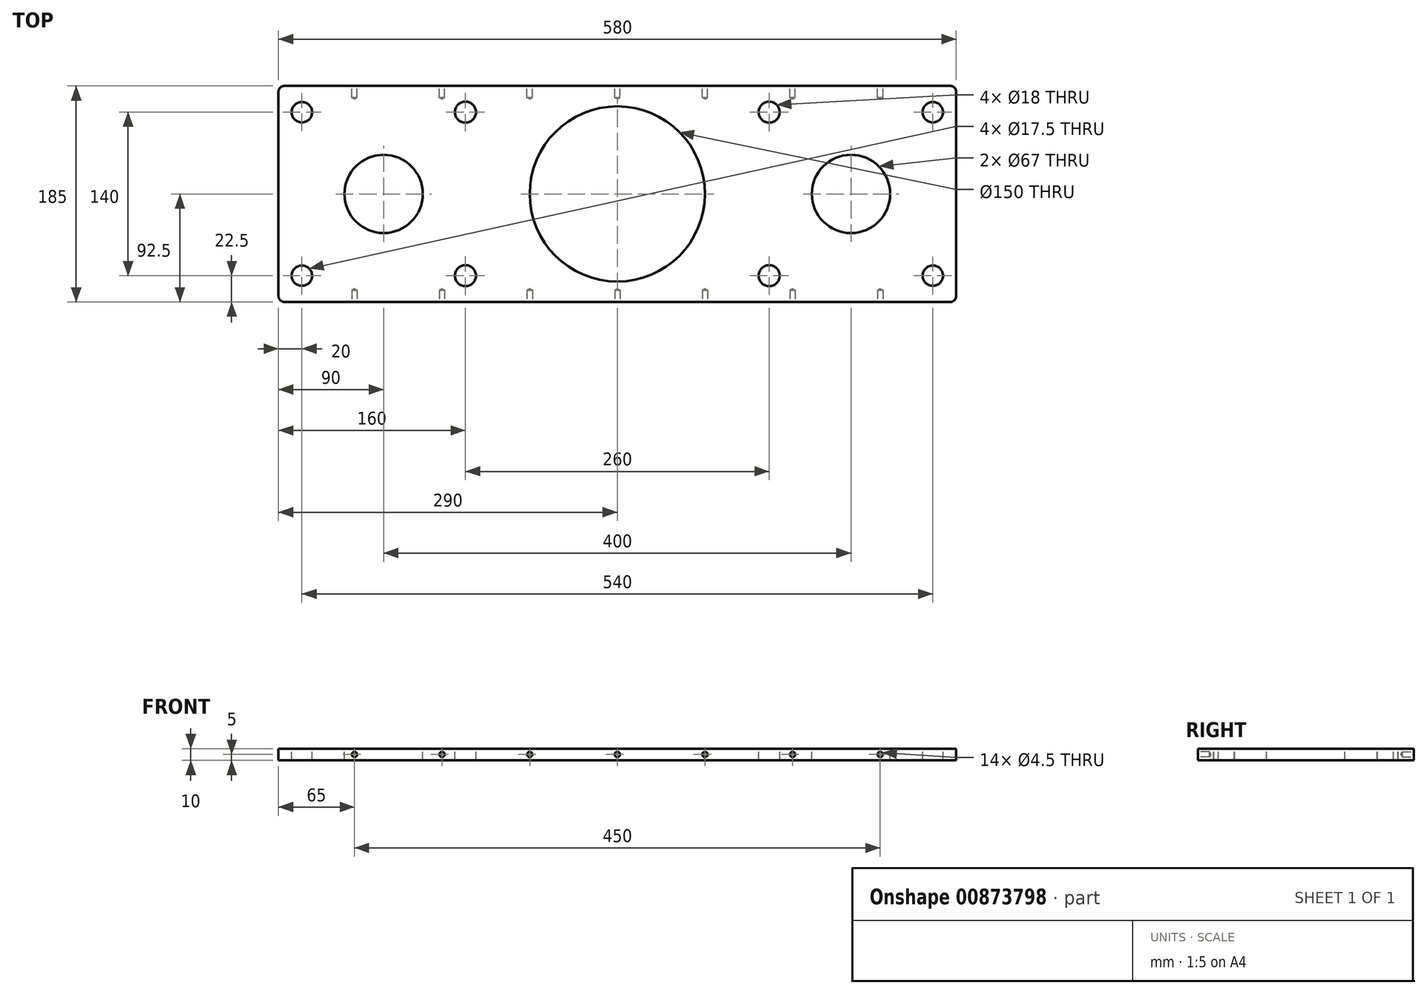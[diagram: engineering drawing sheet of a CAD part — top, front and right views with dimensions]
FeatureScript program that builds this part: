
annotation { "Feature Type Name" : "Feature", "Feature Type Description" : "" }
export const myFeature = defineFeature(function(context is Context, id is Id, definition is map)
    precondition{}
    {
        {
            var Q0;
            Q0=qCreatedBy(makeId("Top.planeOp"),FACE);
            var sketch = newSketch(context, id + "F0", { "sketchPlane" : qUnion([Q0])});
            skLineSegment(sketch, "E0.bottom", {"start": v(290, -92.5) * mm, "end": v(-290, -92.5) * mm});
            skLineSegment(sketch, "E0.top", {"start": v(290, 92.5) * mm, "end": v(-290, 92.5) * mm});
            skLineSegment(sketch, "E0.left", {"start": v(290, -92.5) * mm, "end": v(290, 92.5) * mm});
            skLineSegment(sketch, "E0.right", {"start": v(-290, -92.5) * mm, "end": v(-290, 92.5) * mm});
            skPoint(sketch, "E0.middle", {"position": v(0, 0) * mm});
            skLineSegment(sketch, "E1.bottom", {"start": v(-270, -70) * mm, "end": v(-130, -70) * mm});
            skLineSegment(sketch, "E1.top", {"start": v(-270, 70) * mm, "end": v(-130, 70) * mm});
            skLineSegment(sketch, "E1.left", {"start": v(-270, -70) * mm, "end": v(-270, 70) * mm});
            skLineSegment(sketch, "E1.right", {"start": v(-130, -70) * mm, "end": v(-130, 70) * mm, "construction": true});
            skPoint(sketch, "E1.middle", {"position": v(-200, 0) * mm});
            skLineSegment(sketch, "E2.bottom", {"start": v(130, -70) * mm, "end": v(270, -70) * mm});
            skLineSegment(sketch, "E2.top", {"start": v(130, 70) * mm, "end": v(270, 70) * mm});
            skLineSegment(sketch, "E2.left", {"start": v(130, -70) * mm, "end": v(130, 70) * mm, "construction": true});
            skLineSegment(sketch, "E2.right", {"start": v(270, -70) * mm, "end": v(270, 70) * mm});
            skPoint(sketch, "E2.middle", {"position": v(200, 0) * mm});
            skCircle(sketch, "E3", {"center": v(-200, 0) * mm, "radius": 33.5 * mm});
            skCircle(sketch, "E4", {"center": v(200, 0) * mm, "radius": 33.5 * mm});
            skCircle(sketch, "E5", {"center": v(130, 70) * mm, "radius": 9 * mm});
            skCircle(sketch, "E6", {"center": v(130, -70) * mm, "radius": 9 * mm});
            skCircle(sketch, "E7", {"center": v(270, -70) * mm, "radius": 9 * mm});
            skCircle(sketch, "E8", {"center": v(270, 70) * mm, "radius": 9 * mm});
            skCircle(sketch, "E9", {"center": v(-270, 70) * mm, "radius": 9 * mm});
            skCircle(sketch, "E10", {"center": v(-130, 70) * mm, "radius": 9 * mm});
            skCircle(sketch, "E11", {"center": v(-130, -70) * mm, "radius": 9 * mm});
            skCircle(sketch, "E12", {"center": v(-270, -70) * mm, "radius": 9 * mm});
            skCircle(sketch, "E13", {"center": v(0, 0) * mm, "radius": 75 * mm});
            skLineSegment(sketch, "E14", {"start": v(-200, 0) * mm, "end": v(0, 0) * mm, "construction": true});
            skLineSegment(sketch, "E15", {"start": v(200, 0) * mm, "end": v(0, 0) * mm});
            skCircle(sketch, "E16", {"center": v(0, 0) * mm, "radius": 88.5 * mm, "construction": true});
            skSolve(sketch);
        }
        {
            var Q0;
            Q0=makeQuery(id+"F0.imprint","IMPRINT",FACE,{"disambiguationData":[TD([[makeQuery(id+"F0.imprint","IMPRINT",EDGE,{"derivedFrom":sQuery(id+"F0.wireOp",EDGE,"E0.bottom")}),-1.0]])]});
            var Q1;
            {var subQ0=sQuery(id+"F0.wireOp",EDGE,"E1.right");var subQ1=sQuery(id+"F0.wireOp",EDGE,"E1.top");var subQ2=makeQuery(id+"F0.imprint","INTERSECT",VERTEX,{"derivedFrom":[subQ1,subQ0]});Q1=makeQuery(id+"F0.imprint","IMPRINT",FACE,{"disambiguationData":[TD([[makeQuery(id+"F0.imprint","IMPRINT",EDGE,{"disambiguationData":[TD([[subQ2,1.0]])],"derivedFrom":subQ1}),1.0]])]});}
            var Q2;
            Q2=makeQuery(id+"F0.imprint","IMPRINT",FACE,{"disambiguationData":[TD([[makeQuery(id+"F0.imprint","IMPRINT",EDGE,{"derivedFrom":sQuery(id+"F0.wireOp",EDGE,"E3")}),-1.0]])]});
            var Q3;
            {var subQ0=sQuery(id+"F0.wireOp",EDGE,"E1.left");var subQ1=sQuery(id+"F0.wireOp",EDGE,"E1.top");var subQ2=makeQuery(id+"F0.imprint","INTERSECT",VERTEX,{"derivedFrom":[subQ1,subQ0]});Q3=makeQuery(id+"F0.imprint","IMPRINT",FACE,{"disambiguationData":[TD([[makeQuery(id+"F0.imprint","IMPRINT",EDGE,{"disambiguationData":[TD([[subQ2,-1.0]])],"derivedFrom":subQ1}),1.0]])]});}
            var Q4;
            {var subQ0=sQuery(id+"F0.wireOp",EDGE,"E1.left");var subQ1=sQuery(id+"F0.wireOp",EDGE,"E1.top");var subQ2=makeQuery(id+"F0.imprint","INTERSECT",VERTEX,{"derivedFrom":[subQ1,subQ0]});Q4=makeQuery(id+"F0.imprint","IMPRINT",FACE,{"disambiguationData":[TD([[makeQuery(id+"F0.imprint","IMPRINT",EDGE,{"disambiguationData":[TD([[subQ2,-1.0]])],"derivedFrom":subQ1}),-1.0]])]});}
            var Q5;
            {var subQ0=sQuery(id+"F0.wireOp",EDGE,"E1.right");var subQ1=sQuery(id+"F0.wireOp",EDGE,"E1.top");var subQ2=makeQuery(id+"F0.imprint","INTERSECT",VERTEX,{"derivedFrom":[subQ1,subQ0]});Q5=makeQuery(id+"F0.imprint","IMPRINT",FACE,{"disambiguationData":[TD([[makeQuery(id+"F0.imprint","IMPRINT",EDGE,{"disambiguationData":[TD([[subQ2,1.0]])],"derivedFrom":subQ1}),-1.0]])]});}
            var Q6;
            {var subQ0=sQuery(id+"F0.wireOp",EDGE,"E1.right");var subQ1=sQuery(id+"F0.wireOp",EDGE,"E1.bottom");var subQ2=makeQuery(id+"F0.imprint","INTERSECT",VERTEX,{"derivedFrom":[subQ1,subQ0]});Q6=makeQuery(id+"F0.imprint","IMPRINT",FACE,{"disambiguationData":[TD([[makeQuery(id+"F0.imprint","IMPRINT",EDGE,{"disambiguationData":[TD([[subQ2,1.0]])],"derivedFrom":subQ1}),-1.0]])]});}
            var Q7;
            {var subQ0=sQuery(id+"F0.wireOp",EDGE,"E1.left");var subQ1=sQuery(id+"F0.wireOp",EDGE,"E1.bottom");var subQ2=makeQuery(id+"F0.imprint","INTERSECT",VERTEX,{"derivedFrom":[subQ1,subQ0]});Q7=makeQuery(id+"F0.imprint","IMPRINT",FACE,{"disambiguationData":[TD([[makeQuery(id+"F0.imprint","IMPRINT",EDGE,{"disambiguationData":[TD([[subQ2,-1.0]])],"derivedFrom":subQ1}),1.0]])]});}
            var Q8;
            {var subQ0=sQuery(id+"F0.wireOp",EDGE,"E2.right");var subQ1=sQuery(id+"F0.wireOp",EDGE,"E2.top");var subQ2=makeQuery(id+"F0.imprint","INTERSECT",VERTEX,{"derivedFrom":[subQ1,subQ0]});Q8=makeQuery(id+"F0.imprint","IMPRINT",FACE,{"disambiguationData":[TD([[makeQuery(id+"F0.imprint","IMPRINT",EDGE,{"disambiguationData":[TD([[subQ2,1.0]])],"derivedFrom":subQ1}),-1.0]])]});}
            var Q9;
            {var subQ0=sQuery(id+"F0.wireOp",EDGE,"E2.left");var subQ1=sQuery(id+"F0.wireOp",EDGE,"E2.top");var subQ2=makeQuery(id+"F0.imprint","INTERSECT",VERTEX,{"derivedFrom":[subQ1,subQ0]});Q9=makeQuery(id+"F0.imprint","IMPRINT",FACE,{"disambiguationData":[TD([[makeQuery(id+"F0.imprint","IMPRINT",EDGE,{"disambiguationData":[TD([[subQ2,-1.0]])],"derivedFrom":subQ1}),-1.0]])]});}
            var Q10;
            {var subQ0=sQuery(id+"F0.wireOp",EDGE,"E2.left");var subQ1=sQuery(id+"F0.wireOp",EDGE,"E2.bottom");var subQ2=makeQuery(id+"F0.imprint","INTERSECT",VERTEX,{"derivedFrom":[subQ1,subQ0]});Q10=makeQuery(id+"F0.imprint","IMPRINT",FACE,{"disambiguationData":[TD([[makeQuery(id+"F0.imprint","IMPRINT",EDGE,{"disambiguationData":[TD([[subQ2,-1.0]])],"derivedFrom":subQ1}),-1.0]])]});}
            var Q11;
            {var subQ0=sQuery(id+"F0.wireOp",EDGE,"E2.right");var subQ1=sQuery(id+"F0.wireOp",EDGE,"E2.bottom");var subQ2=makeQuery(id+"F0.imprint","INTERSECT",VERTEX,{"derivedFrom":[subQ1,subQ0]});Q11=makeQuery(id+"F0.imprint","IMPRINT",FACE,{"disambiguationData":[TD([[makeQuery(id+"F0.imprint","IMPRINT",EDGE,{"disambiguationData":[TD([[subQ2,1.0]])],"derivedFrom":subQ1}),1.0]])]});}
            var Q12;
            {var subQ0=sQuery(id+"F0.wireOp",EDGE,"E1.right");var subQ1=sQuery(id+"F0.wireOp",EDGE,"E1.bottom");var subQ2=makeQuery(id+"F0.imprint","INTERSECT",VERTEX,{"derivedFrom":[subQ1,subQ0]});Q12=makeQuery(id+"F0.imprint","IMPRINT",FACE,{"disambiguationData":[TD([[makeQuery(id+"F0.imprint","IMPRINT",EDGE,{"disambiguationData":[TD([[subQ2,1.0]])],"derivedFrom":subQ1}),1.0]])]});}
            var Q13;
            {var subQ0=sQuery(id+"F0.wireOp",EDGE,"E1.left");var subQ1=sQuery(id+"F0.wireOp",EDGE,"E1.bottom");var subQ2=makeQuery(id+"F0.imprint","INTERSECT",VERTEX,{"derivedFrom":[subQ1,subQ0]});Q13=makeQuery(id+"F0.imprint","IMPRINT",FACE,{"disambiguationData":[TD([[makeQuery(id+"F0.imprint","IMPRINT",EDGE,{"disambiguationData":[TD([[subQ2,-1.0]])],"derivedFrom":subQ1}),-1.0]])]});}
            var Q14;
            {var subQ0=sQuery(id+"F0.wireOp",EDGE,"E2.right");var subQ1=sQuery(id+"F0.wireOp",EDGE,"E2.bottom");var subQ2=makeQuery(id+"F0.imprint","INTERSECT",VERTEX,{"derivedFrom":[subQ1,subQ0]});Q14=makeQuery(id+"F0.imprint","IMPRINT",FACE,{"disambiguationData":[TD([[makeQuery(id+"F0.imprint","IMPRINT",EDGE,{"disambiguationData":[TD([[subQ2,1.0]])],"derivedFrom":subQ1}),-1.0]])]});}
            var Q15;
            {var subQ0=sQuery(id+"F0.wireOp",EDGE,"E2.left");var subQ1=sQuery(id+"F0.wireOp",EDGE,"E2.top");var subQ2=makeQuery(id+"F0.imprint","INTERSECT",VERTEX,{"derivedFrom":[subQ1,subQ0]});Q15=makeQuery(id+"F0.imprint","IMPRINT",FACE,{"disambiguationData":[TD([[makeQuery(id+"F0.imprint","IMPRINT",EDGE,{"disambiguationData":[TD([[subQ2,-1.0]])],"derivedFrom":subQ1}),1.0]])]});}
            var Q16;
            {var subQ0=sQuery(id+"F0.wireOp",EDGE,"E2.right");var subQ1=sQuery(id+"F0.wireOp",EDGE,"E2.top");var subQ2=makeQuery(id+"F0.imprint","INTERSECT",VERTEX,{"derivedFrom":[subQ1,subQ0]});Q16=makeQuery(id+"F0.imprint","IMPRINT",FACE,{"disambiguationData":[TD([[makeQuery(id+"F0.imprint","IMPRINT",EDGE,{"disambiguationData":[TD([[subQ2,1.0]])],"derivedFrom":subQ1}),1.0]])]});}
            var Q17;
            {var subQ0=sQuery(id+"F0.wireOp",EDGE,"E2.left");var subQ1=sQuery(id+"F0.wireOp",EDGE,"E2.bottom");var subQ2=makeQuery(id+"F0.imprint","INTERSECT",VERTEX,{"derivedFrom":[subQ1,subQ0]});Q17=makeQuery(id+"F0.imprint","IMPRINT",FACE,{"disambiguationData":[TD([[makeQuery(id+"F0.imprint","IMPRINT",EDGE,{"disambiguationData":[TD([[subQ2,-1.0]])],"derivedFrom":subQ1}),1.0]])]});}
            var Q18;
            Q18=makeQuery(id+"F0.imprint","IMPRINT",FACE,{"disambiguationData":[TD([[makeQuery(id+"F0.imprint","IMPRINT",EDGE,{"derivedFrom":sQuery(id+"F0.wireOp",EDGE,"E4")}),-1.0]])]});
            var Q19;
            Q19=makeQuery(id+"F0.imprint","IMPRINT",FACE,{"disambiguationData":[TD([[makeQuery(id+"F0.imprint","IMPRINT",EDGE,{"derivedFrom":sQuery(id+"F0.wireOp",EDGE,"E13")}),-1.0]])]});
            var Q20;
            {var subQ0=sQuery(id+"F0.wireOp",EDGE,"E10");var subQ1=sQuery(id+"F0.wireOp",EDGE,"E0.top");var subQ2=makeQuery(id+"F0.imprint","INTERSECT",VERTEX,{"disambiguationData":[OD(1.0)],"derivedFrom":[subQ1,subQ0]});Q20=makeQuery(id+"F0.imprint","IMPRINT",FACE,{"disambiguationData":[TD([[makeQuery(id+"F0.imprint","IMPRINT",EDGE,{"disambiguationData":[TD([[subQ2,-1.0]])],"derivedFrom":subQ1}),1.0]])]});}
            var Q21;
            {var subQ0=sQuery(id+"F0.wireOp",EDGE,"E8");var subQ1=sQuery(id+"F0.wireOp",EDGE,"E0.top");var subQ2=makeQuery(id+"F0.imprint","INTERSECT",VERTEX,{"disambiguationData":[OD(1.0)],"derivedFrom":[subQ1,subQ0]});Q21=makeQuery(id+"F0.imprint","IMPRINT",FACE,{"disambiguationData":[TD([[makeQuery(id+"F0.imprint","IMPRINT",EDGE,{"disambiguationData":[TD([[subQ2,-1.0]])],"derivedFrom":subQ1}),1.0]])]});}
            var Q22;
            {var subQ5=sQuery(id+"F0.wireOp",EDGE,"E0.left");Q22=makeQuery(id+"F0.imprint","IMPRINT",FACE,{"disambiguationData":[TD([[makeQuery(id+"F0.imprint","IMPRINT",EDGE,{"derivedFrom":subQ5}),1.0]])]});}
            var Q23;
            {var subQ0=sQuery(id+"F0.wireOp",EDGE,"E0.right");Q23=makeQuery(id+"F0.imprint","IMPRINT",FACE,{"disambiguationData":[TD([[makeQuery(id+"F0.imprint","IMPRINT",EDGE,{"derivedFrom":subQ0}),-1.0]])]});}
            extrude(context, id + "F1", {"entities" : qUnion([Q0, Q1, Q2, Q3, Q4, Q5, Q6, Q7, Q8, Q9, Q10, Q11, Q12, Q13, Q14, Q15, Q16, Q17, Q18, Q19, Q20, Q21, Q22, Q23]), "oppositeDirection" : true, "depth" : 10 * mm, "offsetDistance" : 25 * mm});
        }
        {
            var Q0;
            Q0=sQuery(id+"F0.wireOp",VERTEX,"E1.bottom.start");
            var Q1;
            Q1=sQuery(id+"F0.wireOp",VERTEX,"E1.bottom.end");
            var Q2;
            Q2=sQuery(id+"F0.wireOp",VERTEX,"E1.top.end");
            var Q3;
            Q3=sQuery(id+"F0.wireOp",VERTEX,"E1.top.start");
            var Q4;
            Q4=sQuery(id+"F0.wireOp",VERTEX,"E2.bottom.start");
            var Q5;
            Q5=sQuery(id+"F0.wireOp",VERTEX,"E2.bottom.end");
            var Q6;
            Q6=sQuery(id+"F0.wireOp",VERTEX,"E2.top.end");
            var Q7;
            Q7=sQuery(id+"F0.wireOp",VERTEX,"E2.top.start");
            var Q8;
            Q8=makeQuery(id+"F1.opExtrude","SWEPT_BODY",BODY,{"disambiguationData":[OSD([sQuery(id+"F0.wireOp",EDGE,"E0.bottom"),sQuery(id+"F0.wireOp",EDGE,"E0.top"),sQuery(id+"F0.wireOp",EDGE,"E0.left"),sQuery(id+"F0.wireOp",EDGE,"E0.right"),sQuery(id+"F0.wireOp",EDGE,"E3"),sQuery(id+"F0.wireOp",EDGE,"E4"),sQuery(id+"F0.wireOp",EDGE,"E13")])]});
            hole(context, id + "F2", {"style" : HoleStyle.SIMPLE, "endStyle" : HoleEndStyle.BLIND, "standardTappedOrClearance" : lookupTablePath({ "fit" : "Normal", "standard" : "ISO", "size" : "M16", "type" : "Clearance" }), "standardBlindInLast" : lookupTablePath({ "fit" : "Normal", "standard" : "ISO", "engagement" : "75%", "pitch" : "2 mm", "size" : "M16", "type" : "Clearance & tapped" }), "holeDiameter" : 17.5 * mm, "majorDiameter" : 5 * mm, "holeDepth" : 16.5 * mm, "isTappedThrough" : true, "tappedDepth" : 12 * mm, "tapClearance" : 3, "locations" : qUnion([Q0, Q1, Q2, Q3, Q4, Q5, Q6, Q7]), "scope" : qUnion([Q8])});
        }
        {
            var Q0;
            Q0=makeQuery(id+"F1.opExtrude","SWEPT_EDGE",EDGE,{"disambiguationData":[OSD([sQuery(id+"F0.wireOp",EDGE,"E0.bottom"),sQuery(id+"F0.wireOp",EDGE,"E0.left")])]});
            var Q1;
            Q1=makeQuery(id+"F1.opExtrude","SWEPT_EDGE",EDGE,{"disambiguationData":[OSD([sQuery(id+"F0.wireOp",EDGE,"E0.top"),sQuery(id+"F0.wireOp",EDGE,"E0.left")])]});
            var Q2;
            Q2=makeQuery(id+"F1.opExtrude","SWEPT_EDGE",EDGE,{"disambiguationData":[OSD([sQuery(id+"F0.wireOp",EDGE,"E0.bottom"),sQuery(id+"F0.wireOp",EDGE,"E0.right")])]});
            var Q3;
            Q3=makeQuery(id+"F1.opExtrude","SWEPT_EDGE",EDGE,{"disambiguationData":[OSD([sQuery(id+"F0.wireOp",EDGE,"E0.top"),sQuery(id+"F0.wireOp",EDGE,"E0.right")])]});
            fillet(context, id + "F3", {"entities" : qUnion([Q0, Q1, Q2, Q3]), "radius" : 5 * mm, "tangentPropagation" : true, "defaultsChanged" : true, "vertexSettings" : [], "allowEdgeOverflow" : false});
        }
        {
            var Q0;
            Q0=makeQuery(id+"F1.opExtrude","SWEPT_FACE",FACE,{"disambiguationData":[OSD([sQuery(id+"F0.wireOp",EDGE,"E0.bottom")])]});
            var sketch = newSketch(context, id + "F4", { "sketchPlane" : qUnion([Q0])});
            skPoint(sketch, "E17", {"position": v(-225, -5) * mm});
            skPoint(sketch, "E18.1.0.0", {"position": v(-150, -5) * mm});
            skPoint(sketch, "E18.2.0.0", {"position": v(-75, -5) * mm});
            skLineSegment(sketch, "E18.direction1", {"start": v(-225, -5) * mm, "end": v(-150, -5) * mm, "construction": true});
            skPoint(sketch, "E19.0.3.0", {"position": v(0, -5) * mm});
            skPoint(sketch, "E19.0.4.0", {"position": v(75, -5) * mm});
            skPoint(sketch, "E19.0.5.0", {"position": v(150, -5) * mm});
            skPoint(sketch, "E20.0.6.0", {"position": v(225, -5) * mm});
            skSolve(sketch);
        }
        {
            var Q0;
            Q0=sQuery(id+"F4.wireOp",VERTEX,"E17");
            var Q1;
            Q1=sQuery(id+"F4.wireOp",VERTEX,"E18.1.0.0");
            var Q2;
            Q2=sQuery(id+"F4.wireOp",VERTEX,"E18.2.0.0");
            var Q3;
            Q3=sQuery(id+"F4.wireOp",VERTEX,"E19.0.3.0");
            var Q4;
            Q4=sQuery(id+"F4.wireOp",VERTEX,"E19.0.4.0");
            var Q5;
            Q5=sQuery(id+"F4.wireOp",VERTEX,"E19.0.5.0");
            var Q6;
            Q6=sQuery(id+"F4.wireOp",VERTEX,"E20.0.6.0");
            var Q7;
            Q7=makeQuery(id+"F1.opExtrude","SWEPT_BODY",BODY,{"disambiguationData":[OSD([sQuery(id+"F0.wireOp",EDGE,"E0.bottom"),sQuery(id+"F0.wireOp",EDGE,"E0.top"),sQuery(id+"F0.wireOp",EDGE,"E0.left"),sQuery(id+"F0.wireOp",EDGE,"E0.right"),sQuery(id+"F0.wireOp",EDGE,"E3"),sQuery(id+"F0.wireOp",EDGE,"E4"),sQuery(id+"F0.wireOp",EDGE,"E5"),sQuery(id+"F0.wireOp",EDGE,"E6"),sQuery(id+"F0.wireOp",EDGE,"E10"),sQuery(id+"F0.wireOp",EDGE,"E11"),sQuery(id+"F0.wireOp",EDGE,"E13")])]});
            hole(context, id + "F5", {"style" : HoleStyle.SIMPLE, "endStyle" : HoleEndStyle.BLIND, "standardTappedOrClearance" : lookupTablePath({ "fit" : "Normal", "standard" : "ISO", "size" : "M4", "type" : "Clearance" }), "standardBlindInLast" : lookupTablePath({ "fit" : "Normal", "standard" : "ISO", "engagement" : "75%", "pitch" : "0.7 mm", "size" : "M4", "type" : "Clearance & tapped" }), "holeDiameter" : 4.5 * mm, "majorDiameter" : 5 * mm, "holeDepth" : 10 * mm, "isTappedThrough" : true, "tappedDepth" : 12 * mm, "tapClearance" : 3, "locations" : qUnion([Q0, Q1, Q2, Q3, Q4, Q5, Q6]), "scope" : qUnion([Q7])});
        }
        {
            var Q0;
            Q0=makeQuery(id+"F1.opExtrude","SWEPT_FACE",FACE,{"disambiguationData":[OSD([sQuery(id+"F0.wireOp",EDGE,"E0.top")])]});
            var sketch = newSketch(context, id + "F6", { "sketchPlane" : qUnion([Q0])});
            skPoint(sketch, "E21", {"position": v(-225, -5) * mm});
            skPoint(sketch, "E22.1.0.0", {"position": v(-150, -5) * mm});
            skPoint(sketch, "E22.2.0.0", {"position": v(-75, -5) * mm});
            skPoint(sketch, "E22.3.0.0", {"position": v(0, -5) * mm});
            skPoint(sketch, "E22.4.0.0", {"position": v(75, -5) * mm});
            skPoint(sketch, "E22.5.0.0", {"position": v(150, -5) * mm});
            skPoint(sketch, "E22.6.0.0", {"position": v(225, -5) * mm});
            skLineSegment(sketch, "E22.direction1", {"start": v(-225, -5) * mm, "end": v(-150, -5) * mm, "construction": true});
            skSolve(sketch);
        }
        {
            var Q0;
            Q0=sQuery(id+"F6.wireOp",VERTEX,"E21");
            var Q1;
            Q1=sQuery(id+"F6.wireOp",VERTEX,"E22.1.0.0");
            var Q2;
            Q2=sQuery(id+"F6.wireOp",VERTEX,"E22.2.0.0");
            var Q3;
            Q3=sQuery(id+"F6.wireOp",VERTEX,"E22.3.0.0");
            var Q4;
            Q4=sQuery(id+"F6.wireOp",VERTEX,"E22.4.0.0");
            var Q5;
            Q5=sQuery(id+"F6.wireOp",VERTEX,"E22.5.0.0");
            var Q6;
            Q6=sQuery(id+"F6.wireOp",VERTEX,"E22.6.0.0");
            var Q7;
            Q7=makeQuery(id+"F1.opExtrude","SWEPT_BODY",BODY,{"disambiguationData":[OSD([sQuery(id+"F0.wireOp",EDGE,"E0.bottom"),sQuery(id+"F0.wireOp",EDGE,"E0.top"),sQuery(id+"F0.wireOp",EDGE,"E0.left"),sQuery(id+"F0.wireOp",EDGE,"E0.right"),sQuery(id+"F0.wireOp",EDGE,"E3"),sQuery(id+"F0.wireOp",EDGE,"E4"),sQuery(id+"F0.wireOp",EDGE,"E5"),sQuery(id+"F0.wireOp",EDGE,"E6"),sQuery(id+"F0.wireOp",EDGE,"E10"),sQuery(id+"F0.wireOp",EDGE,"E11"),sQuery(id+"F0.wireOp",EDGE,"E13")])]});
            hole(context, id + "F7", {"style" : HoleStyle.SIMPLE, "endStyle" : HoleEndStyle.BLIND, "standardTappedOrClearance" : lookupTablePath({ "fit" : "Normal", "standard" : "ISO", "size" : "M4", "type" : "Clearance" }), "standardBlindInLast" : lookupTablePath({ "fit" : "Normal", "standard" : "ISO", "engagement" : "75%", "pitch" : "0.7 mm", "size" : "M4", "type" : "Clearance & tapped" }), "holeDiameter" : 4.5 * mm, "majorDiameter" : 5 * mm, "holeDepth" : 10 * mm, "isTappedThrough" : true, "tappedDepth" : 12 * mm, "tapClearance" : 3, "locations" : qUnion([Q0, Q1, Q2, Q3, Q4, Q5, Q6]), "scope" : qUnion([Q7])});
        }
    });
